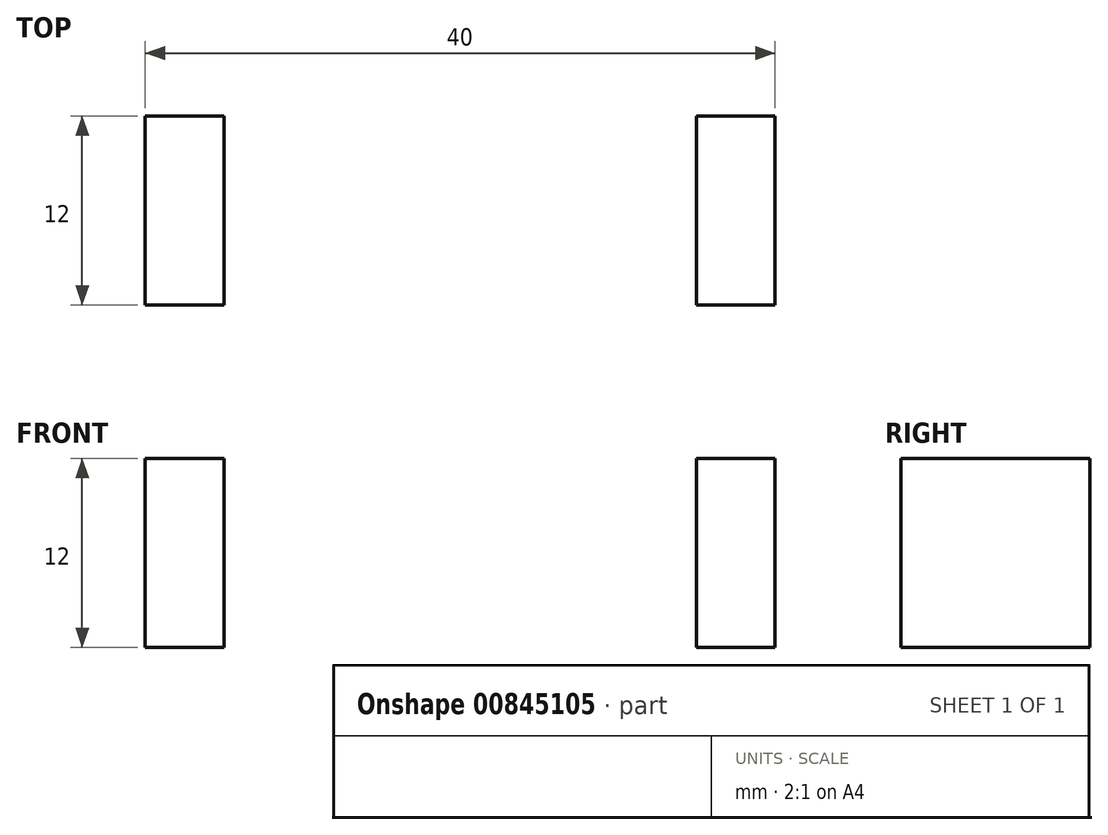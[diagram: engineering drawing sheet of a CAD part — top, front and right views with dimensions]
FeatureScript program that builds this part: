
annotation { "Feature Type Name" : "Feature", "Feature Type Description" : "" }
export const myFeature = defineFeature(function(context is Context, id is Id, definition is map)
    precondition{}
    {
        {
            var Q0;
            Q0=qCreatedBy(makeId("Top.planeOp"),FACE);
            var sketch = newSketch(context, id + "F0", { "sketchPlane" : qUnion([Q0])});
            skLineSegment(sketch, "E0.bottom", {"start": v(0, 0) * mm, "end": v(40, 0) * mm});
            skLineSegment(sketch, "E0.top", {"start": v(0, 424) * mm, "end": v(40, 424) * mm});
            skLineSegment(sketch, "E0.left", {"start": v(0, 0) * mm, "end": v(0, 424) * mm});
            skLineSegment(sketch, "E0.right", {"start": v(40, 0) * mm, "end": v(40, 424) * mm});
            skLineSegment(sketch, "E1.bottom", {"start": v(0, 424) * mm, "end": v(5, 424) * mm});
            skLineSegment(sketch, "E1.top", {"start": v(0, 412) * mm, "end": v(5, 412) * mm});
            skLineSegment(sketch, "E1.left", {"start": v(0, 424) * mm, "end": v(0, 412) * mm});
            skLineSegment(sketch, "E1.right", {"start": v(5, 424) * mm, "end": v(5, 412) * mm});
            skLineSegment(sketch, "E2.bottom", {"start": v(40, 424) * mm, "end": v(35, 424) * mm});
            skLineSegment(sketch, "E2.top", {"start": v(40, 412) * mm, "end": v(35, 412) * mm});
            skLineSegment(sketch, "E2.left", {"start": v(40, 424) * mm, "end": v(40, 412) * mm});
            skLineSegment(sketch, "E2.right", {"start": v(35, 424) * mm, "end": v(35, 412) * mm});
            skLineSegment(sketch, "E3.bottom", {"start": v(0, 0) * mm, "end": v(5, 0) * mm});
            skLineSegment(sketch, "E3.top", {"start": v(0, 12) * mm, "end": v(5, 12) * mm});
            skLineSegment(sketch, "E3.left", {"start": v(0, 0) * mm, "end": v(0, 12) * mm});
            skLineSegment(sketch, "E3.right", {"start": v(5, 0) * mm, "end": v(5, 12) * mm});
            skLineSegment(sketch, "E4.bottom", {"start": v(40, 0) * mm, "end": v(35, 0) * mm});
            skLineSegment(sketch, "E4.top", {"start": v(40, 12) * mm, "end": v(35, 12) * mm});
            skLineSegment(sketch, "E4.left", {"start": v(40, 0) * mm, "end": v(40, 12) * mm});
            skLineSegment(sketch, "E4.right", {"start": v(35, 0) * mm, "end": v(35, 12) * mm});
            skSolve(sketch);
        }
        {
            var Q0;
            Q0=makeQuery(id+"F0.imprint","IMPRINT",FACE,{"disambiguationData":[TD([[makeQuery(id+"F0.imprint","IMPRINT",EDGE,{"derivedFrom":sQuery(id+"F0.wireOp",EDGE,"E0.bottom")}),1.0]])]});
            extrude(context, id + "F1", {"entities" : qUnion([Q0]), "depth" : 12 * mm, "offsetDistance" : 25 * mm});
        }
    });
